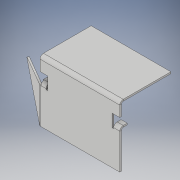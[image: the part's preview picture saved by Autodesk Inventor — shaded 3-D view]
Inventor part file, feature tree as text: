
AUTODESK INVENTOR PART (.ipt)
format: ipt  version: 2019 (Build 230136000, 136)  size: 200,192 bytes
history: native  units: in
note: dims shown in document units (in); Inventor stores cm internally (conversion verified against a paired STEP export)
features: sheet_metal_op x17, other x8, sketch x7
ambient origin geometry x8: Origin, YZ Plane, XZ Plane, XY Plane, X Axis, Y Axis, Z Axis, Center Point
bodies: Solid1 (feature_tree)
feature tree (32):
  sheet_metal_op  "Face1"
  sheet_metal_op  "Face2"
  sheet_metal_op  "Flange2"
  sheet_metal_op  "Flange3"
  sheet_metal_op  "Flange4"
  other  "Corner Chamfer1"
  sheet_metal_op  "Face3"
  sheet_metal_op  "Flange5"
  sketch  "Sketch1"  dims[d0=5.65in]
  other  "Plate1"
  sketch  "Sketch2"  dims[d1=2.75in]
  other  "Plate2"
  sheet_metal_op  "Bend1"
  sketch  "Sketch4"  dims[d2=0.12in]
  other  "Plate4"
  sheet_metal_op  "Bend3"
  sheet_metal_op  "Corner2"
  sketch  "Sketch5"  dims[d3=0.55in]
  other  "Plate5"
  sheet_metal_op  "Bend4"
  sheet_metal_op  "Corner3"
  sketch  "Sketch6"  dims[d4=0.55in]
  other  "Plate6"
  sheet_metal_op  "Bend5"
  sheet_metal_op  "Corner4"
  sketch  "Sketch7"  dims[d5=0.6in]
  other  "Plate7"
  sheet_metal_op  "Bend6"
  sketch  "Sketch8"  dims[d6=0.12in d7=0.12in d8=0.06in d9=0.24in d10=0.12in d21=0.12in d22=0.06in d23=0.24in d24=0.12in d25=0.4in d26=90.0deg d27=0.12in d28=0.48in d29=0.12in d30=0.12in d31=0.12in d32=0.06in d33=0.24in d34=0.12in d35=0.4in d36=90.0deg d37=0.12in d38=0.48in d39=0.12in d40=0.12in d41=0.12in d42=0.06in d43=0.24in d44=0.12in d45=2.5in d46=30.0deg d47=0.12in d48=0.48in d49=0.12in d50=0.12in d51=2.45in d52=0.25in d53=45.0deg d54=0.0in d55=5.65in d56=1.0in d57=0.12in d58=0.12in d59=0.06in d60=0.24in d61=0.12in d62=0.12in d63=0.06in d64=0.24in d65=0.12in d66=3.5in d67=90.0deg d68=0.12in d69=0.48in d70=0.12in d71=0.12in]
  other  "Plate8"
  sheet_metal_op  "Bend7"
  sheet_metal_op  "Corner5"
